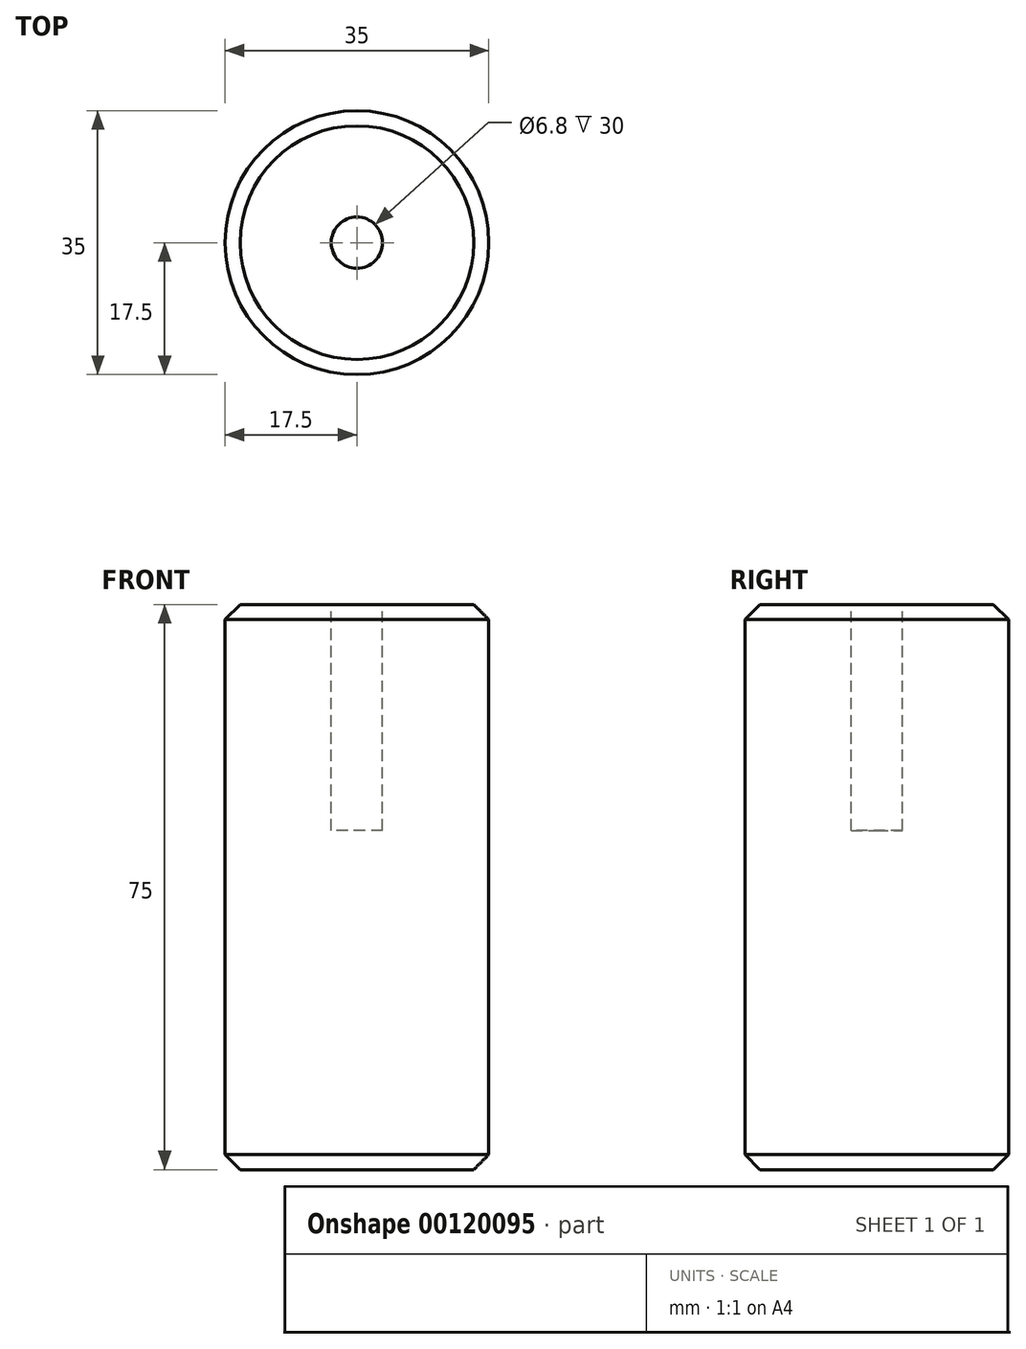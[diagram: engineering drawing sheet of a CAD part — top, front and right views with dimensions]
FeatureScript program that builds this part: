
annotation { "Feature Type Name" : "Feature", "Feature Type Description" : "" }
export const myFeature = defineFeature(function(context is Context, id is Id, definition is map)
    precondition{}
    {
        {
            var Q0;
            Q0=qCreatedBy(makeId("Top.planeOp"),FACE);
            var sketch = newSketch(context, id + "F0", { "sketchPlane" : qUnion([Q0])});
            skCircle(sketch, "E0", {"center": v(0, 0) * mm, "radius": 17.5 * mm});
            skSolve(sketch);
        }
        {
            var Q0;
            Q0 = qSketchRegion(id + "F0", true);
            extrude(context, id + "F1", {"entities" : qUnion([Q0]), "endBound" : BoundingType.SYMMETRIC, "depth" : 75 * mm});
        }
        {
            var Q0;
            Q0=makeQuery(id+"F1.opExtrude","CAP_FACE",FACE,{"disambiguationData":[OSD([sQuery(id+"F0.wireOp",EDGE,"E0")])],"isStart":false});
            var sketch = newSketch(context, id + "F2", { "sketchPlane" : qUnion([Q0])});
            skCircle(sketch, "E1", {"center": v(0, 0) * mm, "radius": 4.25 * mm});
            skSolve(sketch);
        }
        {
            var Q0;
            Q0 = qSketchRegion(id + "F2", true);
            extrude(context, id + "F3", {"entities" : qUnion([Q0]), "operationType" : NewBodyOperationType.REMOVE, "oppositeDirection" : true, "depth" : 25 * mm});
        }
        {
            var Q0;
            Q0=makeQuery(id+"F1.opExtrude","CAP_EDGE",EDGE,{"disambiguationData":[OSD([sQuery(id+"F0.wireOp",EDGE,"E0")])],"isStart":false});
            var Q1;
            Q1=makeQuery(id+"F1.opExtrude","CAP_EDGE",EDGE,{"disambiguationData":[OSD([sQuery(id+"F0.wireOp",EDGE,"E0")])],"isStart":true});
            chamfer(context, id + "F4", {"entities" : qUnion([Q0, Q1]), "width" : 2 * mm, "tangentPropagation" : true});
        }
        {
            var Q0;
            Q0=makeQuery(id+"F1.opExtrude","SWEPT_BODY",BODY,{"disambiguationData":[OSD([sQuery(id+"F0.wireOp",EDGE,"E0")])]});
            deleteBodies(context, id + "F5", {"entities" : qUnion([Q0])});
        }
        {
            var Q0;
            Q0=qCreatedBy(makeId("Top.planeOp"),FACE);
            var sketch = newSketch(context, id + "F6", { "sketchPlane" : qUnion([Q0])});
            skCircle(sketch, "E2", {"center": v(0, 0) * mm, "radius": 17.5 * mm});
            skSolve(sketch);
        }
        {
            var Q0;
            Q0 = qSketchRegion(id + "F6", true);
            extrude(context, id + "F7", {"entities" : qUnion([Q0]), "endBound" : BoundingType.SYMMETRIC, "depth" : 75 * mm});
        }
        {
            var Q0;
            Q0=makeQuery(id+"F7.opExtrude","CAP_FACE",FACE,{"disambiguationData":[OSD([sQuery(id+"F6.wireOp",EDGE,"E2")])],"isStart":false});
            var sketch = newSketch(context, id + "F8", { "sketchPlane" : qUnion([Q0])});
            skCircle(sketch, "E3", {"center": v(0, 0) * mm, "radius": 4.25 * mm});
            skSolve(sketch);
        }
        {
            var Q0;
            Q0 = qSketchRegion(id + "F8", true);
            extrude(context, id + "F9", {"entities" : qUnion([Q0]), "operationType" : NewBodyOperationType.REMOVE, "oppositeDirection" : true, "depth" : 30 * mm});
        }
        {
            var Q0;
            Q0=makeQuery(id+"F7.opExtrude","CAP_EDGE",EDGE,{"disambiguationData":[OSD([sQuery(id+"F6.wireOp",EDGE,"E2")])],"isStart":false});
            var Q1;
            Q1=makeQuery(id+"F7.opExtrude","CAP_EDGE",EDGE,{"disambiguationData":[OSD([sQuery(id+"F6.wireOp",EDGE,"E2")])],"isStart":true});
            chamfer(context, id + "F10", {"entities" : qUnion([Q0, Q1]), "width" : 2 * mm, "tangentPropagation" : true});
        }
        {
            var Q0;
            Q0=makeQuery(id+"F7.opExtrude","CAP_FACE",FACE,{"disambiguationData":[OSD([sQuery(id+"F6.wireOp",EDGE,"E2")])],"isStart":false});
            var sketch = newSketch(context, id + "F11", { "sketchPlane" : qUnion([Q0])});
            skCircle(sketch, "E4", {"center": v(0, 0) * mm, "radius": 5.5 * mm});
            skCircle(sketch, "E5", {"center": v(0, 0) * mm, "radius": 3.4 * mm});
            skSolve(sketch);
        }
        {
            var Q0;
            Q0 = qSketchRegion(id + "F11", true);
            extrude(context, id + "F12", {"entities" : qUnion([Q0]), "operationType" : NewBodyOperationType.ADD, "oppositeDirection" : true, "depth" : 30 * mm});
        }
    });
